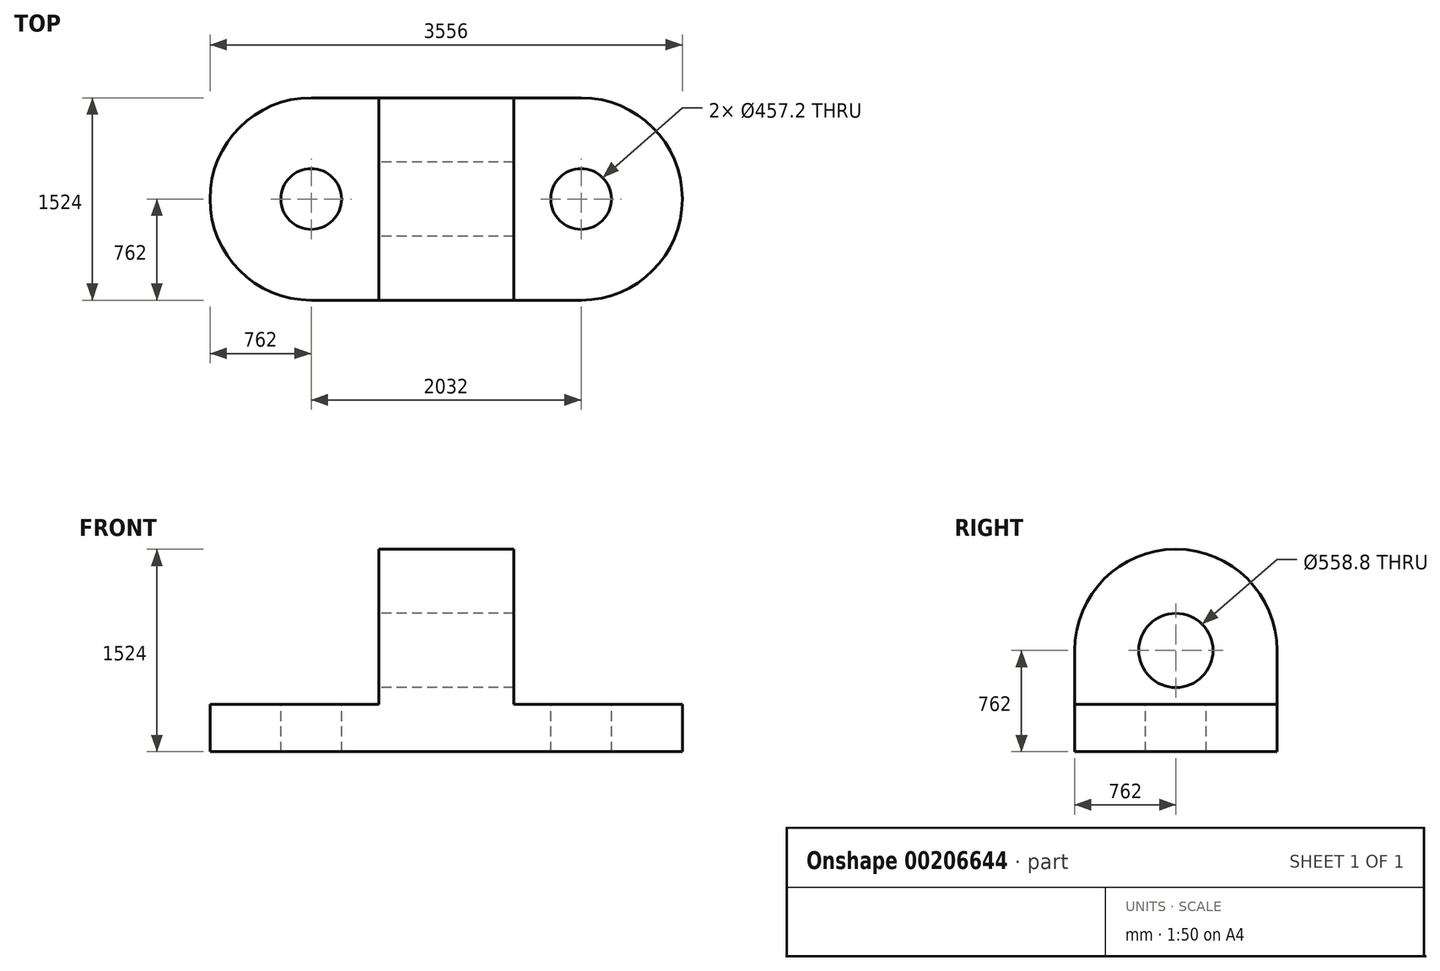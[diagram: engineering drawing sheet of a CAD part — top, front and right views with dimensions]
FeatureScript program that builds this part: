
annotation { "Feature Type Name" : "Feature", "Feature Type Description" : "" }
export const myFeature = defineFeature(function(context is Context, id is Id, definition is map)
    precondition{}
    {
        {
            var Q0;
            Q0=qCreatedBy(makeId("Top.planeOp"),FACE);
            var sketch = newSketch(context, id + "F0", { "sketchPlane" : qUnion([Q0])});
            skLineSegment(sketch, "E0.bottom", {"start": v(0, 0) * mm, "end": v(-3556, 0) * mm});
            skLineSegment(sketch, "E0.top", {"start": v(0, 1524) * mm, "end": v(-3556, 1524) * mm});
            skLineSegment(sketch, "E0.left", {"start": v(0, 0) * mm, "end": v(0, 1524) * mm});
            skLineSegment(sketch, "E0.right", {"start": v(-3556, 0) * mm, "end": v(-3556, 1524) * mm});
            skSolve(sketch);
        }
        {
            var Q0;
            Q0=qSketchRegion(id+"F0",true);
            extrude(context, id + "F1", {"entities" : qUnion([Q0]), "depth" : 355.6 * mm});
        }
        {
            var Q0;
            Q0=makeQuery(id+"F1.opExtrude","CAP_FACE",FACE,{"disambiguationData":[OSD([sQuery(id+"F0.wireOp",EDGE,"E0.bottom"),sQuery(id+"F0.wireOp",EDGE,"E0.top"),sQuery(id+"F0.wireOp",EDGE,"E0.left"),sQuery(id+"F0.wireOp",EDGE,"E0.right")])],"isStart":false});
            var sketch = newSketch(context, id + "F2", { "sketchPlane" : qUnion([Q0])});
            skLineSegment(sketch, "E1.bottom", {"start": v(-2286, 0) * mm, "end": v(-1270, 0) * mm});
            skLineSegment(sketch, "E1.top", {"start": v(-2286, 1524) * mm, "end": v(-1270, 1524) * mm});
            skLineSegment(sketch, "E1.left", {"start": v(-2286, 0) * mm, "end": v(-2286, 1524) * mm});
            skLineSegment(sketch, "E1.right", {"start": v(-1270, 0) * mm, "end": v(-1270, 1524) * mm});
            skSolve(sketch);
        }
        {
            var Q0;
            Q0=makeQuery(id+"F2.imprint","IMPRINT",FACE,{"disambiguationData":[TD([[makeQuery(id+"F2.imprint","IMPRINT",EDGE,{"derivedFrom":sQuery(id+"F2.wireOp",EDGE,"E1.bottom")}),-1.0]])]});
            extrude(context, id + "F3", {"entities" : qUnion([Q0]), "operationType" : NewBodyOperationType.ADD, "depth" : 1168.4 * mm});
        }
        {
            var Q0;
            Q0=makeQuery(id+"F3.opExtrude","CAP_EDGE",EDGE,{"disambiguationData":[OSD([sQuery(id+"F2.wireOp",EDGE,"E1.bottom")])],"isStart":false});
            var Q1;
            Q1=makeQuery(id+"F1.opExtrude","SWEPT_EDGE",EDGE,{"disambiguationData":[OSD([sQuery(id+"F0.wireOp",EDGE,"E0.bottom"),sQuery(id+"F0.wireOp",EDGE,"E0.left")])]});
            var Q2;
            Q2=makeQuery(id+"F1.opExtrude","SWEPT_EDGE",EDGE,{"disambiguationData":[OSD([sQuery(id+"F0.wireOp",EDGE,"E0.top"),sQuery(id+"F0.wireOp",EDGE,"E0.left")])]});
            var Q3;
            Q3=makeQuery(id+"F1.opExtrude","SWEPT_EDGE",EDGE,{"disambiguationData":[OSD([sQuery(id+"F0.wireOp",EDGE,"E0.bottom"),sQuery(id+"F0.wireOp",EDGE,"E0.right")])]});
            var Q4;
            Q4=makeQuery(id+"F1.opExtrude","SWEPT_EDGE",EDGE,{"disambiguationData":[OSD([sQuery(id+"F0.wireOp",EDGE,"E0.top"),sQuery(id+"F0.wireOp",EDGE,"E0.right")])]});
            var Q5;
            Q5=makeQuery(id+"F3.opExtrude","CAP_EDGE",EDGE,{"disambiguationData":[OSD([sQuery(id+"F2.wireOp",EDGE,"E1.top")])],"isStart":false});
            fillet(context, id + "F4", {"entities" : qUnion([Q0, Q1, Q2, Q3, Q4, Q5]), "radius" : 762 * mm, "tangentPropagation" : true, "allowEdgeOverflow" : false});
        }
        {
            var Q0;
            Q0=makeQuery(id+"F3.opExtrude","SWEPT_FACE",FACE,{"disambiguationData":[OSD([sQuery(id+"F2.wireOp",EDGE,"E1.left")])]});
            var sketch = newSketch(context, id + "F5", { "sketchPlane" : qUnion([Q0])});
            skCircle(sketch, "E2", {"center": v(-762, 762) * mm, "radius": 279.4 * mm});
            skSolve(sketch);
        }
        {
            var Q0;
            Q0=makeQuery(id+"F5.imprint","IMPRINT",FACE,{"disambiguationData":[TD([[makeQuery(id+"F5.imprint","IMPRINT",EDGE,{"derivedFrom":sQuery(id+"F5.wireOp",EDGE,"E2")}),1.0]])]});
            extrude(context, id + "F6", {"entities" : qUnion([Q0]), "operationType" : NewBodyOperationType.REMOVE, "oppositeDirection" : true, "depth" : 1016 * mm});
        }
        {
            var Q0;
            {var subQ0=sQuery(id+"F0.wireOp",EDGE,"E0.left");var subQ1=sQuery(id+"F0.wireOp",EDGE,"E0.top");var subQ2=sQuery(id+"F0.wireOp",EDGE,"E0.bottom");Q0=makeQuery(id+"F3.boolean.opBoolean","SPLIT",FACE,{"disambiguationData":[TD([makeQuery(id+"F1.opExtrude","SWEPT_FACE",FACE,{"disambiguationData":[OSD([subQ0])]})])],"derivedFrom":makeQuery(id+"F1.opExtrude","CAP_FACE",FACE,{"disambiguationData":[OSD([subQ2,subQ1,subQ0,sQuery(id+"F0.wireOp",EDGE,"E0.right")])],"isStart":false})});}
            var sketch = newSketch(context, id + "F7", { "sketchPlane" : qUnion([Q0])});
            skCircle(sketch, "E3", {"center": v(-762, 762) * mm, "radius": 228.6 * mm});
            skSolve(sketch);
        }
        {
            var Q0;
            Q0=makeQuery(id+"F7.imprint","IMPRINT",FACE,{"disambiguationData":[TD([[makeQuery(id+"F7.imprint","IMPRINT",EDGE,{"derivedFrom":sQuery(id+"F7.wireOp",EDGE,"E3")}),1.0]])]});
            extrude(context, id + "F8", {"entities" : qUnion([Q0]), "operationType" : NewBodyOperationType.REMOVE, "oppositeDirection" : true, "depth" : 355.6 * mm});
        }
        {
            var Q0;
            {var subQ0=sQuery(id+"F0.wireOp",EDGE,"E0.right");var subQ1=sQuery(id+"F0.wireOp",EDGE,"E0.top");var subQ2=sQuery(id+"F0.wireOp",EDGE,"E0.bottom");Q0=makeQuery(id+"F3.boolean.opBoolean","SPLIT",FACE,{"disambiguationData":[TD([makeQuery(id+"F1.opExtrude","SWEPT_FACE",FACE,{"disambiguationData":[OSD([subQ0])]})])],"derivedFrom":makeQuery(id+"F1.opExtrude","CAP_FACE",FACE,{"disambiguationData":[OSD([subQ2,subQ1,sQuery(id+"F0.wireOp",EDGE,"E0.left"),subQ0])],"isStart":false})});}
            var sketch = newSketch(context, id + "F9", { "sketchPlane" : qUnion([Q0])});
            skCircle(sketch, "E4", {"center": v(-2794, 762) * mm, "radius": 228.6 * mm});
            skSolve(sketch);
        }
        {
            var Q0;
            Q0=makeQuery(id+"F9.imprint","IMPRINT",FACE,{"disambiguationData":[TD([[makeQuery(id+"F9.imprint","IMPRINT",EDGE,{"derivedFrom":sQuery(id+"F9.wireOp",EDGE,"E4")}),1.0]])]});
            extrude(context, id + "F10", {"entities" : qUnion([Q0]), "operationType" : NewBodyOperationType.REMOVE, "oppositeDirection" : true, "depth" : 355.6 * mm});
        }
    });
